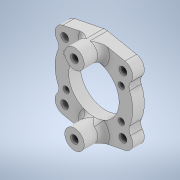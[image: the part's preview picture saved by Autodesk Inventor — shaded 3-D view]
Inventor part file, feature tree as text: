
AUTODESK INVENTOR PART (.ipt)
format: ipt  version: 2020 (Build 240168000, 168)  size: 408,576 bytes
history: native  units: mm
features: projected_geometry x9, sketch x8, extrude x6, other x3, hole x2, fillet x2, thicken_offset x2, plane x1, reference x1
ambient origin geometry x8: Origin, YZ Plane, XZ Plane, XY Plane, X Axis, Y Axis, Z Axis, Center Point
bodies: Solid1 (feature_tree)
feature tree (34):
  extrude  "Extrusion1"  Depth=20.0mm
  plane  "Work Plane1"
  extrude  "Extrusion3"  Depth=15.0mm
  hole  "Hole1"  [1 undecoded]
  fillet  "Fillet5"  Radius=5.0mm
  thicken_offset  "Thicken3"
  thicken_offset  "Thicken4"
  extrude  "Extrusion5"  Depth=4.0mm
  extrude  "Extrusion6"  Depth=1.0mm
  extrude  "Extrusion7"  Depth=1.0mm
  extrude  "Extrusion8"  Depth=4.0mm
  fillet  "Fillet7"  Radius=9.0mm
  hole  "Hole2"  [1 undecoded]
  sketch  "Sketch1"  dims[d0=13.0mm d1=20.0mm]
  reference  "Reference1"
  sketch  "Sketch3"  dims[d2=3.0mm d3=0.0mm d21=15.0mm]
  projected_geometry  "Projected Loop1"
  sketch  "Sketch4"  dims[d22=15.0mm d23=5.0mm d24=5.0mm]
  projected_geometry  "Projected Loop2"
  sketch  "Sketch6"  dims[d25=3.0mm d26=0.0mm]
  projected_geometry  "Projected Loop6"
  sketch  "Sketch7"  dims[d27=2.0mm d28=6.0mm d29=4.0mm d30=2.0mm d31=90.0deg d32=8.0mm d33=20.594885mm d34=2.0mm]
  projected_geometry  "Projected Loop7"
  sketch  "Sketch8"  dims[d35=1.0mm d36=1.0mm]
  projected_geometry  "Projected Loop8"
  sketch  "Sketch9"  dims[d37=1.0mm d38=1.0mm]
  projected_geometry  "Projected Loop9"
  sketch  "Sketch10"  dims[d61=9.0mm d62=5.0mm d63=9.0mm d64=5.0mm d65=10.0mm d66=0.0mm d67=10.0mm d68=0.0mm d69=10.0mm d70=0.0mm d71=5.0mm d72=5.0mm d73=5.0mm d74=0.0mm d75=1.5mm d76=2.0mm d77=6.0mm d78=4.0mm d79=2.0mm d80=90.0deg d81=20.0mm d82=0.0mm]
  projected_geometry  "Projected Loop10"
  projected_geometry  "Projected Loop11"
  projected_geometry  "Projected Loop12"
  other  "Assembly1"
  other  "brushless_20:1"
  other  "burshless_20_base:1"
note: 2 required parameter values undecoded (feature->parameter linkage not recoverable at this tier; creation-order binding heuristic only, values carry confidence <= 0.55)
